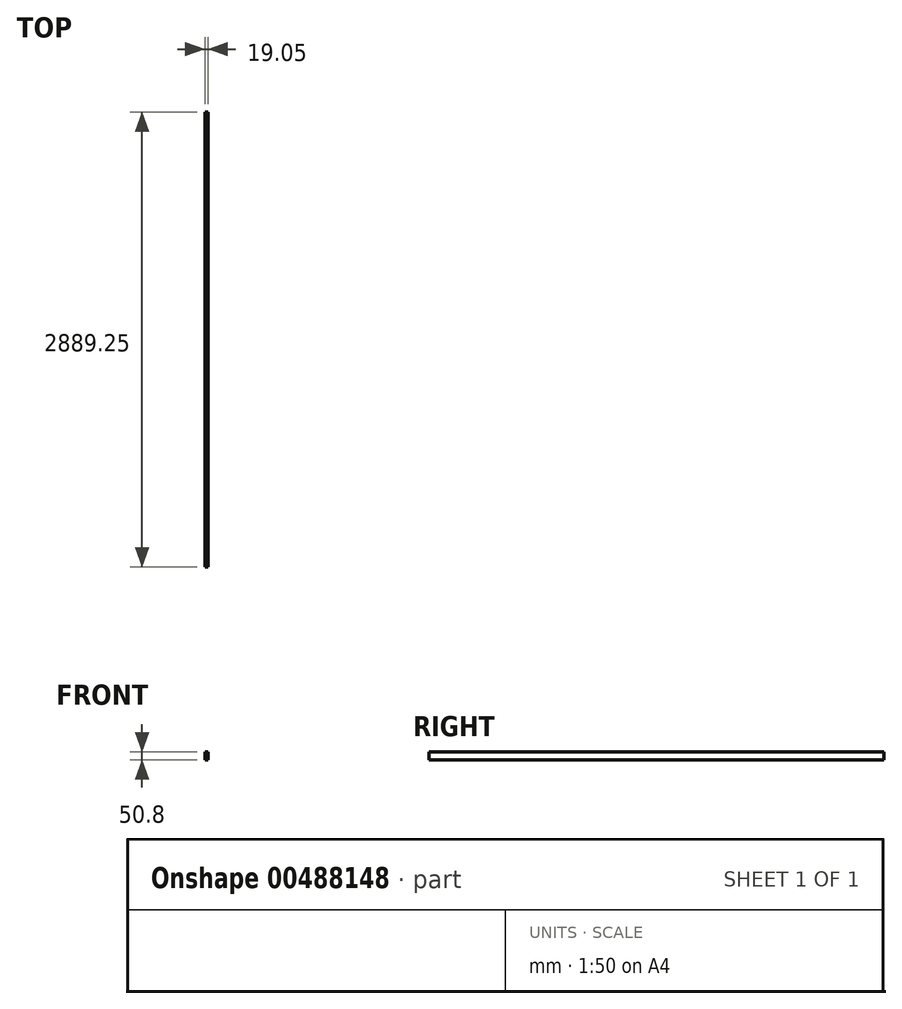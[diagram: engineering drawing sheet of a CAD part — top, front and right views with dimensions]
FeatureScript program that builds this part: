
annotation { "Feature Type Name" : "Feature", "Feature Type Description" : "" }
export const myFeature = defineFeature(function(context is Context, id is Id, definition is map)
    precondition{}
    {
        {
            var Q0;
            Q0=qCreatedBy(makeId("Front.planeOp"),FACE);
            var sketch = newSketch(context, id + "F0", { "sketchPlane" : qUnion([Q0])});
            skLineSegment(sketch, "E0", {"start": v(0, 0) * mm, "end": v(19.05, 0) * mm});
            skLineSegment(sketch, "E1", {"start": v(0, 0) * mm, "end": v(0, -50.8) * mm});
            skLineSegment(sketch, "E2", {"start": v(0, -50.8) * mm, "end": v(19.05, -50.8) * mm});
            skLineSegment(sketch, "E3", {"start": v(19.05, -50.8) * mm, "end": v(19.05, 0) * mm});
            skSolve(sketch);
        }
        {
            var Q0;
            Q0=makeQuery(id+"F0.imprint","IMPRINT",FACE,{"disambiguationData":[TD([[makeQuery(id+"F0.imprint","IMPRINT",EDGE,{"derivedFrom":sQuery(id+"F0.wireOp",EDGE,"E0")}),-1.0]])]});
            extrude(context, id + "F1", {"entities" : qUnion([Q0]), "oppositeDirection" : true, "depth" : 2889.25 * mm, "offsetDistance" : 25.4 * mm});
        }
    });
